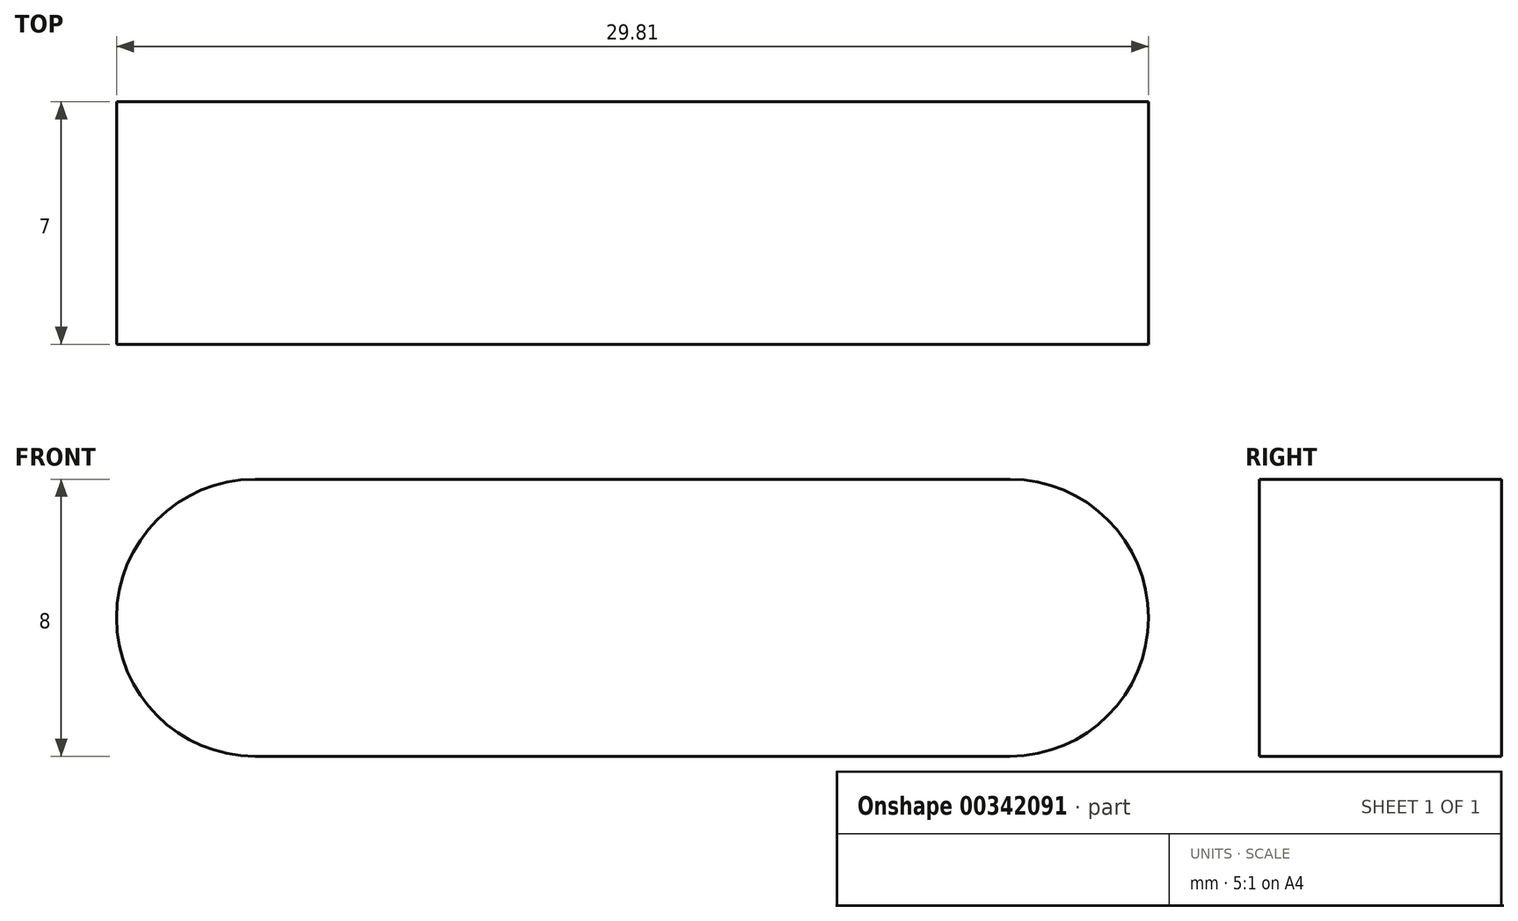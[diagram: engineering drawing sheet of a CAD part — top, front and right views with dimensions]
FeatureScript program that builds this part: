
annotation { "Feature Type Name" : "Feature", "Feature Type Description" : "" }
export const myFeature = defineFeature(function(context is Context, id is Id, definition is map)
    precondition{}
    {
        {
            var Q0;
            Q0=qCreatedBy(makeId("Front.planeOp"),FACE);
            var sketch = newSketch(context, id + "F0", { "sketchPlane" : qUnion([Q0])});
            skLineSegment(sketch, "E0", {"start": v(0, 0) * mm, "end": v(0, 8) * mm});
            skArc(sketch, "E1", {"start": v(0, 8) * mm, "mid": v(-4, 4) * mm, "end": v(0, 0) * mm});
            skLineSegment(sketch, "E2", {"start": v(0, 8) * mm, "end": v(21.8, 8) * mm});
            skLineSegment(sketch, "E3", {"start": v(0, 0) * mm, "end": v(21.8, 0) * mm});
            skLineSegment(sketch, "E4", {"start": v(21.8, 8) * mm, "end": v(21.8, 0) * mm});
            skArc(sketch, "E5", {"start": v(21.8, 0) * mm, "mid": v(25.8, 4) * mm, "end": v(21.8, 8) * mm});
            skSolve(sketch);
        }
        {
            var Q0;
            Q0=qSketchRegion(id+"F0",true);
            extrude(context, id + "F1", {"entities" : qUnion([Q0]), "depth" : 7 * mm});
        }
    });
